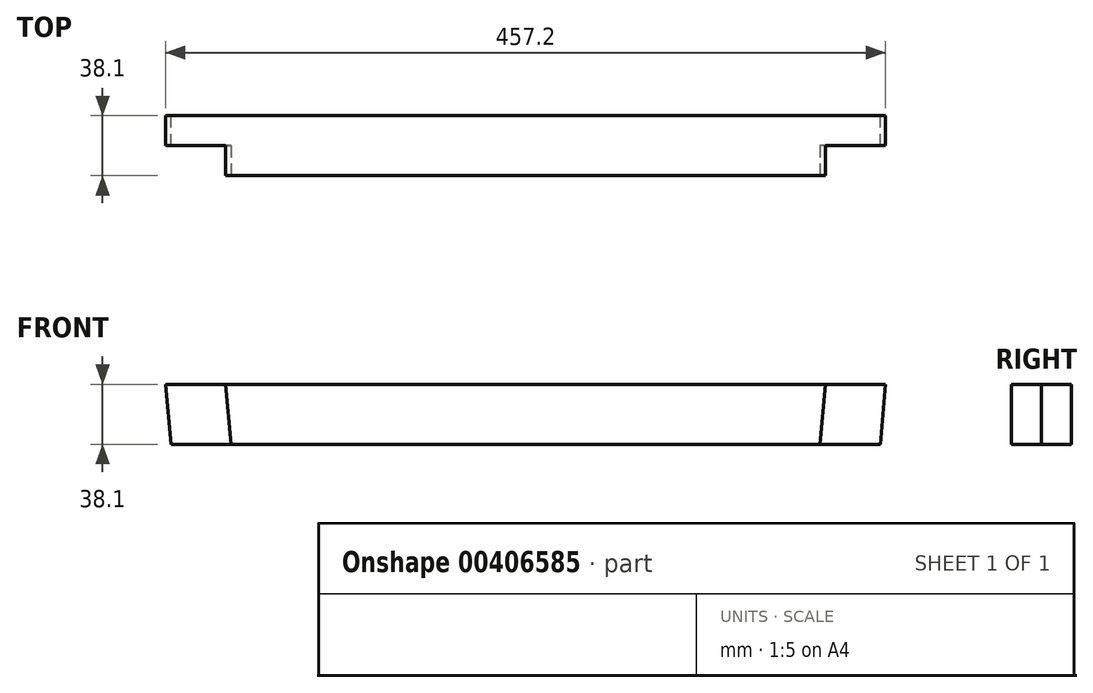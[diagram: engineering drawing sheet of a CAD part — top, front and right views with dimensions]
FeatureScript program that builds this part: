
annotation { "Feature Type Name" : "Feature", "Feature Type Description" : "" }
export const myFeature = defineFeature(function(context is Context, id is Id, definition is map)
    precondition{}
    {
        {
            var Q0;
            Q0=qCreatedBy(makeId("Front.planeOp"),FACE);
            var sketch = newSketch(context, id + "F0", { "sketchPlane" : qUnion([Q0])});
            skLineSegment(sketch, "E0", {"start": v(0, 0) * mm, "end": v(457.2, 0) * mm});
            skLineSegment(sketch, "E1", {"start": v(457.2, 0) * mm, "end": v(453.87, -38.1) * mm});
            skLineSegment(sketch, "E2", {"start": v(453.87, -38.1) * mm, "end": v(3.33, -38.1) * mm});
            skLineSegment(sketch, "E3", {"start": v(3.33, -38.1) * mm, "end": v(0, 0) * mm});
            skSolve(sketch);
        }
        {
            var Q0;
            Q0=makeQuery(id+"F0.imprint","IMPRINT",FACE,{"disambiguationData":[TD([[makeQuery(id+"F0.imprint","IMPRINT",EDGE,{"derivedFrom":sQuery(id+"F0.wireOp",EDGE,"E0")}),-1.0]])]});
            extrude(context, id + "F1", {"entities" : qUnion([Q0]), "depth" : 38.1 * mm});
        }
        {
            var Q0;
            Q0=makeQuery(id+"F1.opExtrude","CAP_FACE",FACE,{"disambiguationData":[OSD([sQuery(id+"F0.wireOp",EDGE,"E0"),sQuery(id+"F0.wireOp",EDGE,"E1"),sQuery(id+"F0.wireOp",EDGE,"E2"),sQuery(id+"F0.wireOp",EDGE,"E3")])],"isStart":false});
            var sketch = newSketch(context, id + "F2", { "sketchPlane" : qUnion([Q0])});
            skLineSegment(sketch, "E4", {"start": v(418.95, 0) * mm, "end": v(415.62, -38.1) * mm});
            skLineSegment(sketch, "E5", {"start": v(418.95, 0) * mm, "end": v(457.2, 0) * mm});
            skLineSegment(sketch, "E6", {"start": v(457.2, 0) * mm, "end": v(453.87, -38.1) * mm});
            skLineSegment(sketch, "E7", {"start": v(453.87, -38.1) * mm, "end": v(415.62, -38.1) * mm});
            skSolve(sketch);
        }
        {
            var Q0;
            Q0=makeQuery(id+"F2.imprint","IMPRINT",FACE,{"disambiguationData":[TD([[makeQuery(id+"F2.imprint","IMPRINT",EDGE,{"derivedFrom":sQuery(id+"F2.wireOp",EDGE,"E4")}),1.0]])]});
            extrude(context, id + "F3", {"entities" : qUnion([Q0]), "operationType" : NewBodyOperationType.REMOVE, "oppositeDirection" : true, "depth" : 19.05 * mm});
        }
        {
            var Q0;
            Q0=makeQuery(id+"F1.opExtrude","CAP_FACE",FACE,{"disambiguationData":[OSD([sQuery(id+"F0.wireOp",EDGE,"E0"),sQuery(id+"F0.wireOp",EDGE,"E1"),sQuery(id+"F0.wireOp",EDGE,"E2"),sQuery(id+"F0.wireOp",EDGE,"E3")])],"isStart":false});
            var sketch = newSketch(context, id + "F4", { "sketchPlane" : qUnion([Q0])});
            skLineSegment(sketch, "E8", {"start": v(38.25, 0) * mm, "end": v(41.58, -38.1) * mm});
            skLineSegment(sketch, "E9", {"start": v(38.25, 0) * mm, "end": v(0, 0) * mm});
            skLineSegment(sketch, "E10", {"start": v(0, 0) * mm, "end": v(3.33, -38.1) * mm});
            skLineSegment(sketch, "E11", {"start": v(3.33, -38.1) * mm, "end": v(41.58, -38.1) * mm});
            skSolve(sketch);
        }
        {
            var Q0;
            Q0=makeQuery(id+"F4.imprint","IMPRINT",FACE,{"disambiguationData":[TD([[makeQuery(id+"F4.imprint","IMPRINT",EDGE,{"derivedFrom":sQuery(id+"F4.wireOp",EDGE,"E8")}),-1.0]])]});
            extrude(context, id + "F5", {"entities" : qUnion([Q0]), "operationType" : NewBodyOperationType.REMOVE, "oppositeDirection" : true, "depth" : 19.05 * mm});
        }
    });
